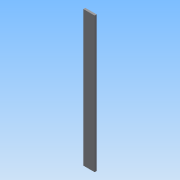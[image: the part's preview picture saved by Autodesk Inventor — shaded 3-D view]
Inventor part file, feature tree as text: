
AUTODESK INVENTOR PART (.ipt)
format: ipt  version: 2015 (Build 190159000, 159)  size: 67,072 bytes
history: native  units: mm
features: extrude x1, sketch x1
ambient origin geometry x8: Origin, YZ Plane, XZ Plane, XY Plane, X Axis, Y Axis, Z Axis, Center Point
bodies: Solid1 (feature_tree)
feature tree (2):
  extrude  "Extrusion1"  Depth=50.0mm
  sketch  "Sketch1"  dims[d0=600.0mm d1=50.0mm d2=9.0mm d3=0.0mm]
